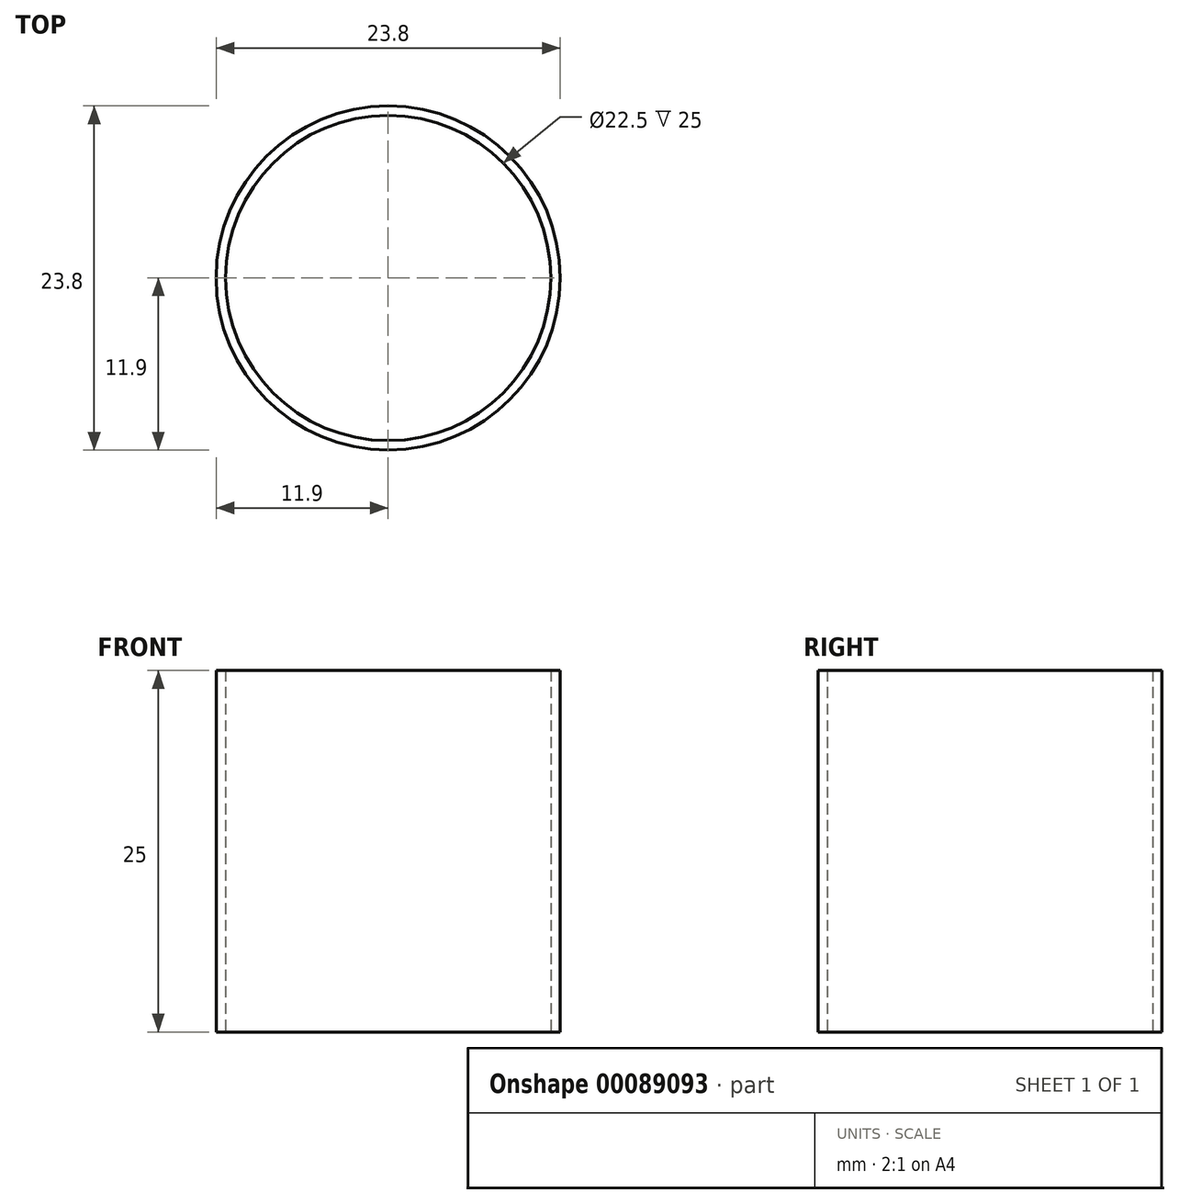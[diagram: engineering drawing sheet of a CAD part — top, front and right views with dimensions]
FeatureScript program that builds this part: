
annotation { "Feature Type Name" : "Feature", "Feature Type Description" : "" }
export const myFeature = defineFeature(function(context is Context, id is Id, definition is map)
    precondition{}
    {
        {
            var Q0;
            Q0=qCreatedBy(makeId("Top.planeOp"),FACE);
            var sketch = newSketch(context, id + "F0", { "sketchPlane" : qUnion([Q0])});
            skCircle(sketch, "E0", {"center": v(0, 0) * mm, "radius": 11.25 * mm});
            skCircle(sketch, "E1", {"center": v(0, 0) * mm, "radius": 11.9 * mm});
            skSolve(sketch);
        }
        {
            var Q0;
            Q0=makeQuery(id+"F0.imprint","IMPRINT",FACE,{"disambiguationData":[TD([[makeQuery(id+"F0.imprint","IMPRINT",EDGE,{"derivedFrom":sQuery(id+"F0.wireOp",EDGE,"E0")}),-1.0]])]});
            extrude(context, id + "F1", {"entities" : qUnion([Q0]), "depth" : 25 * mm});
        }
    });
